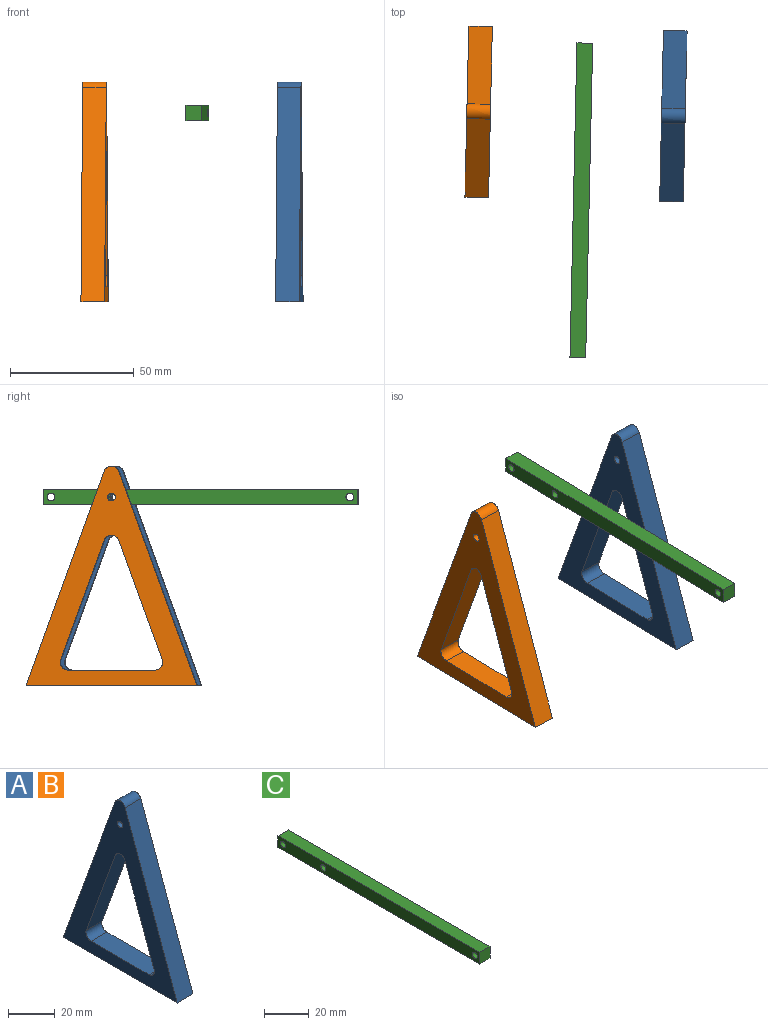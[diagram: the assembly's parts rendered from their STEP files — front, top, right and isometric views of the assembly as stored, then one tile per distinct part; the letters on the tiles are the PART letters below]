
ASSEMBLY  parts=3 mates=2
PART A: 13 faces, bbox 9.5x69x88.7 mm
  f0: plane 48.11x17.51mm, normal (0,0.94,-0.34), area 487.6mm2, adj f1,f9,f10,f11
  f1: cylinder r=3.17mm len=9.53mm, axis (-1,0,0), area 73.9mm2, adj f0,f2,f10,f11
  f2: plane 48.11x17.51mm, normal (0,-0.94,-0.34), area 487.6mm2, adj f1,f3,f10,f11
  f3: cylinder r=3.17mm len=9.53mm, axis (-1,0,0), area 58.1mm2, adj f2,f4,f10,f11
  f4: plane 35.02x9.53mm, normal (0,0,1), area 333.6mm2, adj f3,f9,f10,f11
  f5: plane 68.98x9.53mm, normal (0,0,-1), area 657.1mm2, adj f6,f8,f10,f11
  f6: plane 86.57x31.51mm, normal (0,0.94,0.34), area 877.5mm2, adj f5,f7,f10,f11
  f7: cylinder r=3.17mm len=9.53mm, axis (-1,0,0), area 73.9mm2, adj f6,f8,f10,f11
  f8: plane 86.57x31.51mm, normal (0,-0.94,0.34), area 877.5mm2, adj f5,f7,f10,f11
  f9: cylinder r=3.17mm len=9.53mm, axis (-1,0,0), area 58.1mm2, adj f0,f4,f10,f11
  f10: plane 88.66x68.98mm, normal (1,0,0), area 1935mm2, adj f0,f1,f2,f3,f4,f5,f6,f7
  f11: plane 88.66x68.98mm, normal (-1,0,0), area 1935mm2, adj f0,f1,f2,f3,f4,f5,f6,f7
  f12: cylinder r=1.59mm len=9.53mm, axis (-1,0,0), area 95mm2, adj f10,f11
PART B: same geometry as A
PART C: 9 faces, bbox 6.4x127x6.4 mm
  f0: plane 127x6.35mm, normal (0,0,1), area 806.5mm2, adj f1,f3,f4,f5
  f1: plane 6.35x6.35mm, normal (0,-1,0), area 40.3mm2, adj f0,f2,f4,f5
  f2: plane 127x6.35mm, normal (0,0,-1), area 806.5mm2, adj f1,f3,f4,f5
  f3: plane 6.35x6.35mm, normal (0,1,0), area 40.3mm2, adj f0,f2,f4,f5
  f4: plane 127x6.35mm, normal (1,0,0), area 782.7mm2, adj f0,f1,f2,f3,f6,f7,f8
  f5: plane 127x6.35mm, normal (-1,0,0), area 782.7mm2, adj f0,f1,f2,f3,f6,f7,f8
  f6: cylinder r=1.59mm len=6.35mm, axis (1,0,0), area 63.3mm2, adj f4,f5
  f7: cylinder r=1.59mm len=6.35mm, axis (1,0,0), area 63.3mm2, adj f4,f5
  f8: cylinder r=1.59mm len=6.35mm, axis (1,0,0), area 63.3mm2, adj f4,f5
PLACE A rot(axis=(0,0,-1),1.3deg) t=(66.2,-8.67,0)mm
PLACE B rot(axis=(0,0,-1),1.3deg) t=(-12.38,-6.92,0)mm
PLACE C rot(axis=(0,0,-1),1.3deg) t=(34.59,-7.97,76.2)mm
MATE cylindrical B.f12 <-> C.f6  axis (-1,0.02,0) through (-2.86,-7.13,76.2)mm
MATE planar B.f5 <-> A.f5  axis (0,0,-1) through (-7.62,-7.03,0)mm
